# Revit family: NBS_TapcoRoofingProducts_DryFxngVrgs_TapcoSlate_DryVerge
name_source: partatom
category: Generic Models
units: mm (PartAtom-declared; Revit-internal decimal feet)

## family parameters
Always vertical = Yes
Can host rebar = No
Cut with Voids When Loaded = No
Part Type = Normal
Room Calculation Point = No
Round Connector Dimension = Use Diameter
Shared = No
Work Plane-Based = No

## types (1)
- TapcoSlate_DryVerge
    Applications = Suitable for use with Tapco Slate Classic products, designed for use with most natural and man-made tiles
    AssetType = Fixed
    BIMObjectName = NBS_TapcoRoofingProducts_DryFixingVerges_TapcoSlate_DryVerge
    Category = Pr_35_90_93_30:Dry fixing verges
    Color = Black
    Combustible = Yes
    Description = A dry-fix slate/ shake dry verge system installed on gable ends securing slates protecting the verge from wind uplift and the elements
    DryVergeLength = 2000 mm  [stored 6.56168 ft]
    DryVergeMaterial = NBS_TapcoRoofingProducts_PVC-U_Black
    DurationUnit = year
    ExpectedLife = 25+ years
    Features = Wind uplift and rain protection, patented ‘Drip System’ which allows for self drainage of rain water into the gutter, requires no maintenance once installed, jointing clip also available, easy and quick to install
    IfcExportAs = IfcCoveringType
    IfcExportType = ROOFING
    IsExternal = Yes
    ManufacturerName = Tapco Roofing Products
    ManufacturerURL = www.tapcoroofingproducts.com
    Material = Unplasticised polyvinyl chloride (PVC-U)
    ModelReference = TapcoSlate_DryVerge
    NBSCertification = www.nationalbimlibrary.com/cert/jr2tk03y
    NBSDescription = Dry fixing verges
    NBSReference = 45-80-90/378
    Name = DryFixingVerges_TapcoSlate_DryVerge_TapcoRoofingProducts
    NominalHeight = 73 mm
    NominalLength = 2000 mm  [stored 6.56168 ft]
    NominalWidth = 90 mm
    ProductInformation = https://www.tapcoroofingproducts.com
    Shape = Rectangular
    Size = 73 x 2000 x 90 mm
    Status = UNSET
    ThermalTransmittance = 0
    Uniclass2015Code = Pr_35_90_93_30
    Uniclass2015Title = Dry fixing verges
    Uniclass2015Version = Products v1.20
    Version = 1
    WarrantyDescription = 40-years
    WarrantyDurationUnit = year

note: [stored X ft] marks values corroborated as IEEE doubles in the binary element streams (Revit-internal decimal feet)

## geometry (parser evidence)
native form markers: Sweep x2
no freeform markers — native parametric forms only
